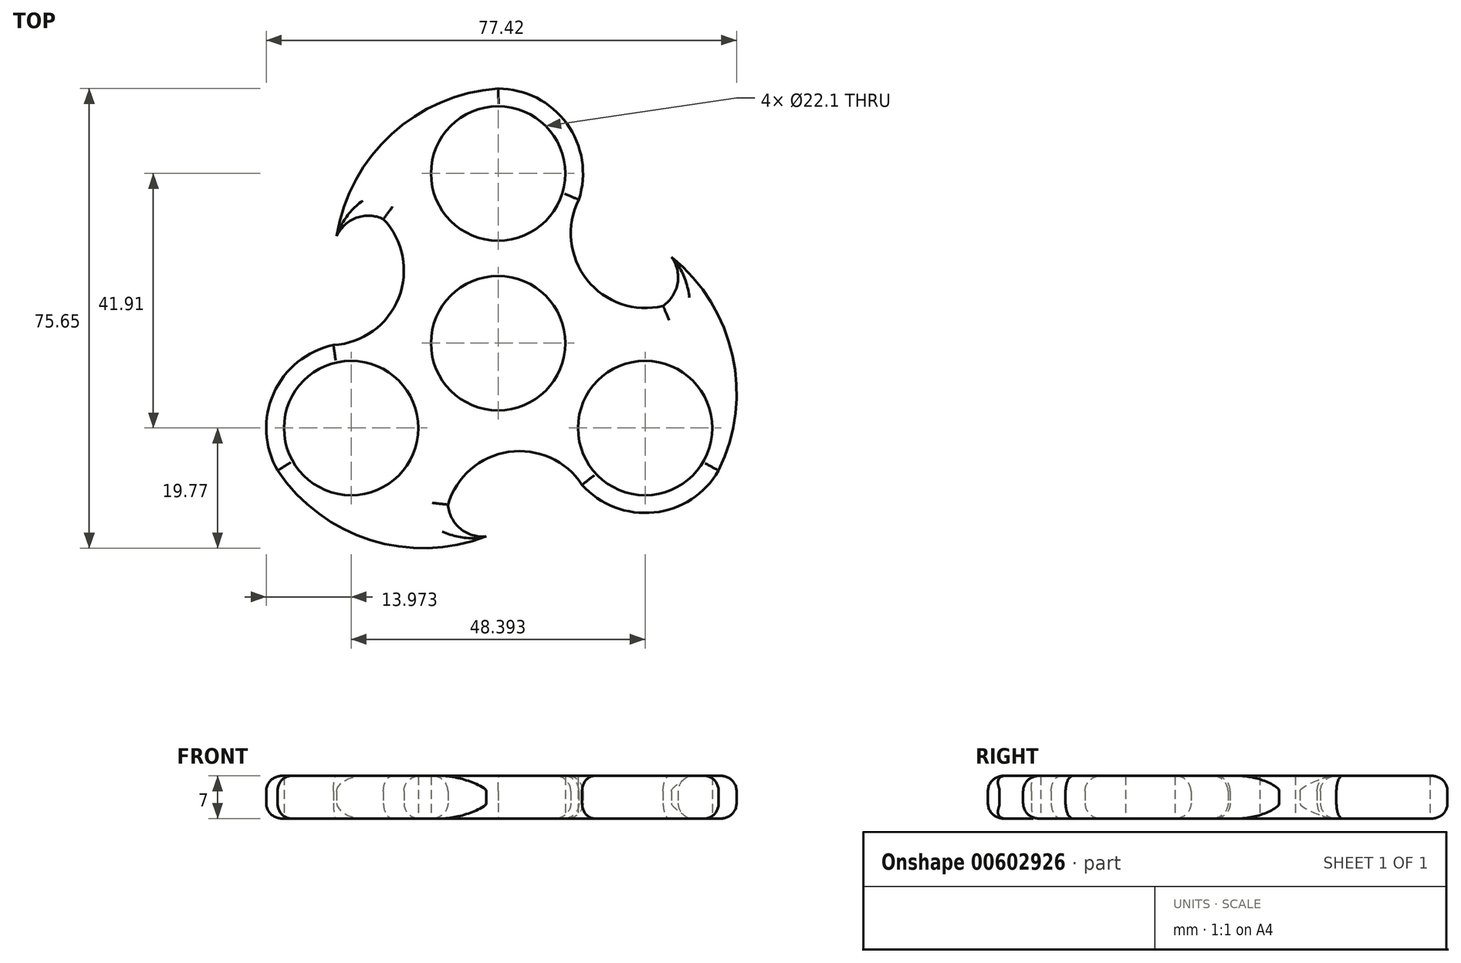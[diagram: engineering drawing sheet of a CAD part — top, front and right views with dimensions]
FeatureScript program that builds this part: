
annotation { "Feature Type Name" : "Feature", "Feature Type Description" : "" }
export const myFeature = defineFeature(function(context is Context, id is Id, definition is map)
    precondition{}
    {
        {
            var Q0;
            Q0=qCreatedBy(makeId("Top.planeOp"),FACE);
            var sketch = newSketch(context, id + "F0", { "sketchPlane" : qUnion([Q0])});
            skCircle(sketch, "E0", {"center": v(0, 0) * mm, "radius": 11.05 * mm});
            skCircle(sketch, "E1", {"center": v(0, 27.94) * mm, "radius": 11.05 * mm});
            skCircle(sketch, "E2.1.0", {"center": v(-24.2, -13.97) * mm, "radius": 11.05 * mm});
            skCircle(sketch, "E2.2.0", {"center": v(24.2, -13.97) * mm, "radius": 11.05 * mm});
            skArc(sketch, "E3", {"start": v(12.54, 21.78) * mm, "mid": v(10.8, 36.8) * mm, "end": v(-3.59, 41.44) * mm});
            skArc(sketch, "E4", {"start": v(-25.13, -0.03) * mm, "mid": v(-37.27, -9.05) * mm, "end": v(-34.1, -23.83) * mm});
            skArc(sketch, "E5", {"start": v(12.6, -21.75) * mm, "mid": v(26.47, -27.75) * mm, "end": v(37.68, -17.61) * mm});
            skPoint(sketch, "E6.start.orphan", {"position": v(0, 41.91) * mm});
            skArc(sketch, "E7", {"start": v(-18.88, 20.44) * mm, "mid": v(-23.33, 20.64) * mm, "end": v(-26.57, 17.6) * mm});
            skPoint(sketch, "E8.startSnap0", {"position": v(-15.2, 14.45) * mm});
            skArc(sketch, "E9", {"start": v(0, 41.91) * mm, "mid": v(-17.55, 34.4) * mm, "end": v(-26.57, 17.6) * mm});
            skArc(sketch, "E10.1.0", {"start": v(-36.3, -20.95) * mm, "mid": v(-21.03, -32.4) * mm, "end": v(-1.95, -31.81) * mm});
            skArc(sketch, "E10.1.1", {"start": v(-8.26, -26.57) * mm, "mid": v(-6.21, -30.52) * mm, "end": v(-1.95, -31.81) * mm});
            skArc(sketch, "E10.2.0", {"start": v(36.3, -20.96) * mm, "mid": v(38.57, -2) * mm, "end": v(28.53, 14.22) * mm});
            skArc(sketch, "E10.2.1", {"start": v(27.14, 6.14) * mm, "mid": v(29.54, 9.88) * mm, "end": v(28.53, 14.22) * mm});
            skArc(sketch, "E11", {"start": v(13.81, -23.32) * mm, "mid": v(1.74, -17.9) * mm, "end": v(-8.26, -26.57) * mm});
            skArc(sketch, "E12.1.0", {"start": v(13.29, 23.62) * mm, "mid": v(14.63, 10.46) * mm, "end": v(27.14, 6.14) * mm});
            skArc(sketch, "E12.2.0", {"start": v(-27.1, -0.3) * mm, "mid": v(-16.37, 7.44) * mm, "end": v(-18.88, 20.44) * mm});
            skPoint(sketch, "E13.end.orphan", {"position": v(-15.2, 4.25) * mm});
            skSolve(sketch);
        }
        {
            var Q0;
            Q0=makeQuery(id+"F0.imprint","IMPRINT",FACE,{"disambiguationData":[TD([[makeQuery(id+"F0.imprint","IMPRINT",EDGE,{"derivedFrom":sQuery(id+"F0.wireOp",EDGE,"E1")}),-1.0]])]});
            var Q1;
            Q1=makeQuery(id+"F0.imprint","IMPRINT",FACE,{"disambiguationData":[TD([[makeQuery(id+"F0.imprint","IMPRINT",EDGE,{"derivedFrom":sQuery(id+"F0.wireOp",EDGE,"E2.2.0")}),-1.0]])]});
            var Q2;
            Q2=makeQuery(id+"F0.imprint","IMPRINT",FACE,{"disambiguationData":[TD([[makeQuery(id+"F0.imprint","IMPRINT",EDGE,{"derivedFrom":sQuery(id+"F0.wireOp",EDGE,"E2.1.0")}),-1.0]])]});
            var Q3;
            Q3=makeQuery(id+"F0.imprint","IMPRINT",FACE,{"disambiguationData":[TD([[makeQuery(id+"F0.imprint","IMPRINT",EDGE,{"derivedFrom":sQuery(id+"F0.wireOp",EDGE,"4O9khdKf-2qk6-6eEU-YUye-EU3OGTiNBHui")}),-1.0]])]});
            var Q4;
            Q4=makeQuery(id+"F0.imprint","IMPRINT",FACE,{"disambiguationData":[TD([[makeQuery(id+"F0.imprint","IMPRINT",EDGE,{"derivedFrom":sQuery(id+"F0.wireOp",EDGE,"E0")}),-1.0]])]});
            extrude(context, id + "F1", {"entities" : qUnion([Q0, Q1, Q2, Q3, Q4]), "depth" : 7 * mm, "offsetDistance" : 25 * mm});
        }
        {
            var Q0;
            Q0=makeQuery(id+"F1.opExtrude","CAP_EDGE",EDGE,{"disambiguationData":[OSD([sQuery(id+"F0.wireOp",EDGE,"E10.1.0")])],"isStart":false});
            var Q1;
            Q1=makeQuery(id+"F1.opExtrude","CAP_EDGE",EDGE,{"disambiguationData":[OSD([sQuery(id+"F0.wireOp",EDGE,"E8")])],"isStart":false});
            var Q2;
            Q2=makeQuery(id+"F1.opExtrude","CAP_EDGE",EDGE,{"disambiguationData":[OSD([sQuery(id+"F0.wireOp",EDGE,"E13")])],"isStart":false});
            var Q3;
            Q3=makeQuery(id+"F1.opExtrude","CAP_EDGE",EDGE,{"disambiguationData":[OSD([sQuery(id+"F0.wireOp",EDGE,"E9")])],"isStart":false});
            var Q4;
            Q4=makeQuery(id+"F1.opExtrude","CAP_EDGE",EDGE,{"disambiguationData":[OSD([sQuery(id+"F0.wireOp",EDGE,"E3")])],"isStart":false});
            var Q5;
            Q5=makeQuery(id+"F1.opExtrude","CAP_EDGE",EDGE,{"disambiguationData":[OSD([sQuery(id+"F0.wireOp",EDGE,"E10.2.3")])],"isStart":false});
            var Q6;
            Q6=makeQuery(id+"F1.opExtrude","CAP_EDGE",EDGE,{"disambiguationData":[OSD([sQuery(id+"F0.wireOp",EDGE,"E10.2.2")])],"isStart":false});
            var Q7;
            Q7=makeQuery(id+"F1.opExtrude","CAP_EDGE",EDGE,{"disambiguationData":[OSD([sQuery(id+"F0.wireOp",EDGE,"E10.2.1")])],"isStart":false});
            var Q8;
            Q8=makeQuery(id+"F1.opExtrude","CAP_EDGE",EDGE,{"disambiguationData":[OSD([sQuery(id+"F0.wireOp",EDGE,"E10.1.2")])],"isStart":false});
            var Q9;
            Q9=makeQuery(id+"F1.opExtrude","CAP_EDGE",EDGE,{"disambiguationData":[OSD([sQuery(id+"F0.wireOp",EDGE,"E10.1.1")])],"isStart":false});
            var Q10;
            Q10=makeQuery(id+"F1.opExtrude","CAP_EDGE",EDGE,{"disambiguationData":[OSD([sQuery(id+"F0.wireOp",EDGE,"E10.2.0")])],"isStart":false});
            var Q11;
            Q11=makeQuery(id+"F1.opExtrude","CAP_EDGE",EDGE,{"disambiguationData":[OSD([sQuery(id+"F0.wireOp",EDGE,"E10.1.3")])],"isStart":false});
            var Q12;
            Q12=makeQuery(id+"F1.opExtrude","CAP_EDGE",EDGE,{"disambiguationData":[OSD([sQuery(id+"F0.wireOp",EDGE,"E7")])],"isStart":false});
            var Q13;
            Q13=makeQuery(id+"F1.opExtrude","CAP_EDGE",EDGE,{"disambiguationData":[OSD([sQuery(id+"F0.wireOp",EDGE,"E10.2.0")])],"isStart":true});
            var Q14;
            Q14=makeQuery(id+"F1.opExtrude","CAP_EDGE",EDGE,{"disambiguationData":[OSD([sQuery(id+"F0.wireOp",EDGE,"E10.2.2")])],"isStart":true});
            var Q15;
            Q15=makeQuery(id+"F1.opExtrude","CAP_EDGE",EDGE,{"disambiguationData":[OSD([sQuery(id+"F0.wireOp",EDGE,"E10.2.3")])],"isStart":true});
            var Q16;
            Q16=makeQuery(id+"F1.opExtrude","CAP_EDGE",EDGE,{"disambiguationData":[OSD([sQuery(id+"F0.wireOp",EDGE,"E9")])],"isStart":true});
            var Q17;
            Q17=makeQuery(id+"F1.opExtrude","CAP_EDGE",EDGE,{"disambiguationData":[OSD([sQuery(id+"F0.wireOp",EDGE,"E8")])],"isStart":true});
            var Q18;
            Q18=makeQuery(id+"F1.opExtrude","CAP_EDGE",EDGE,{"disambiguationData":[OSD([sQuery(id+"F0.wireOp",EDGE,"E13")])],"isStart":true});
            var Q19;
            Q19=makeQuery(id+"F1.opExtrude","CAP_EDGE",EDGE,{"disambiguationData":[OSD([sQuery(id+"F0.wireOp",EDGE,"E10.1.0")])],"isStart":true});
            var Q20;
            Q20=makeQuery(id+"F1.opExtrude","CAP_EDGE",EDGE,{"disambiguationData":[OSD([sQuery(id+"F0.wireOp",EDGE,"E10.1.1")])],"isStart":true});
            var Q21;
            Q21=makeQuery(id+"F1.opExtrude","CAP_EDGE",EDGE,{"disambiguationData":[OSD([sQuery(id+"F0.wireOp",EDGE,"E10.1.2")])],"isStart":true});
            var Q22;
            Q22=makeQuery(id+"F1.opExtrude","CAP_EDGE",EDGE,{"disambiguationData":[OSD([sQuery(id+"F0.wireOp",EDGE,"E10.1.3")])],"isStart":true});
            var Q23;
            Q23=makeQuery(id+"F1.opExtrude","CAP_EDGE",EDGE,{"disambiguationData":[OSD([sQuery(id+"F0.wireOp",EDGE,"E11")])],"isStart":true});
            var Q24;
            Q24=makeQuery(id+"F1.opExtrude","CAP_EDGE",EDGE,{"disambiguationData":[OSD([sQuery(id+"F0.wireOp",EDGE,"E5")])],"isStart":true});
            var Q25;
            Q25=makeQuery(id+"F1.opExtrude","CAP_EDGE",EDGE,{"disambiguationData":[OSD([sQuery(id+"F0.wireOp",EDGE,"E5")])],"isStart":false});
            var Q26;
            Q26=makeQuery(id+"F1.opExtrude","CAP_EDGE",EDGE,{"disambiguationData":[OSD([sQuery(id+"F0.wireOp",EDGE,"E11")])],"isStart":false});
            var Q27;
            Q27=makeQuery(id+"F1.opExtrude","CAP_EDGE",EDGE,{"disambiguationData":[OSD([sQuery(id+"F0.wireOp",EDGE,"E12.2.0")])],"isStart":false});
            var Q28;
            Q28=makeQuery(id+"F1.opExtrude","CAP_EDGE",EDGE,{"disambiguationData":[OSD([sQuery(id+"F0.wireOp",EDGE,"E4")])],"isStart":false});
            var Q29;
            Q29=makeQuery(id+"F1.opExtrude","CAP_EDGE",EDGE,{"disambiguationData":[OSD([sQuery(id+"F0.wireOp",EDGE,"E12.1.0")])],"isStart":false});
            var Q30;
            Q30=makeQuery(id+"F1.opExtrude","CAP_EDGE",EDGE,{"disambiguationData":[OSD([sQuery(id+"F0.wireOp",EDGE,"E12.2.0")])],"isStart":true});
            var Q31;
            Q31=makeQuery(id+"F1.opExtrude","CAP_EDGE",EDGE,{"disambiguationData":[OSD([sQuery(id+"F0.wireOp",EDGE,"E7")])],"isStart":true});
            var Q32;
            Q32=makeQuery(id+"F1.opExtrude","CAP_EDGE",EDGE,{"disambiguationData":[OSD([sQuery(id+"F0.wireOp",EDGE,"E4")])],"isStart":true});
            var Q33;
            Q33=makeQuery(id+"F1.opExtrude","CAP_EDGE",EDGE,{"disambiguationData":[OSD([sQuery(id+"F0.wireOp",EDGE,"E3")])],"isStart":true});
            var Q34;
            Q34=makeQuery(id+"F1.opExtrude","CAP_EDGE",EDGE,{"disambiguationData":[OSD([sQuery(id+"F0.wireOp",EDGE,"E12.1.0")])],"isStart":true});
            var Q35;
            Q35=makeQuery(id+"F1.opExtrude","CAP_EDGE",EDGE,{"disambiguationData":[OSD([sQuery(id+"F0.wireOp",EDGE,"E10.2.1")])],"isStart":true});
            fillet(context, id + "F2", {"entities" : qUnion([Q0, Q1, Q2, Q3, Q4, Q5, Q6, Q7, Q8, Q9, Q10, Q11, Q12, Q13, Q14, Q15, Q16, Q17, Q18, Q19, Q20, Q21, Q22, Q23, Q24, Q25, Q26, Q27, Q28, Q29, Q30, Q31, Q32, Q33, Q34, Q35]), "radius" : 2.54 * mm, "tangentPropagation" : true, "allowEdgeOverflow" : false});
        }
    });
